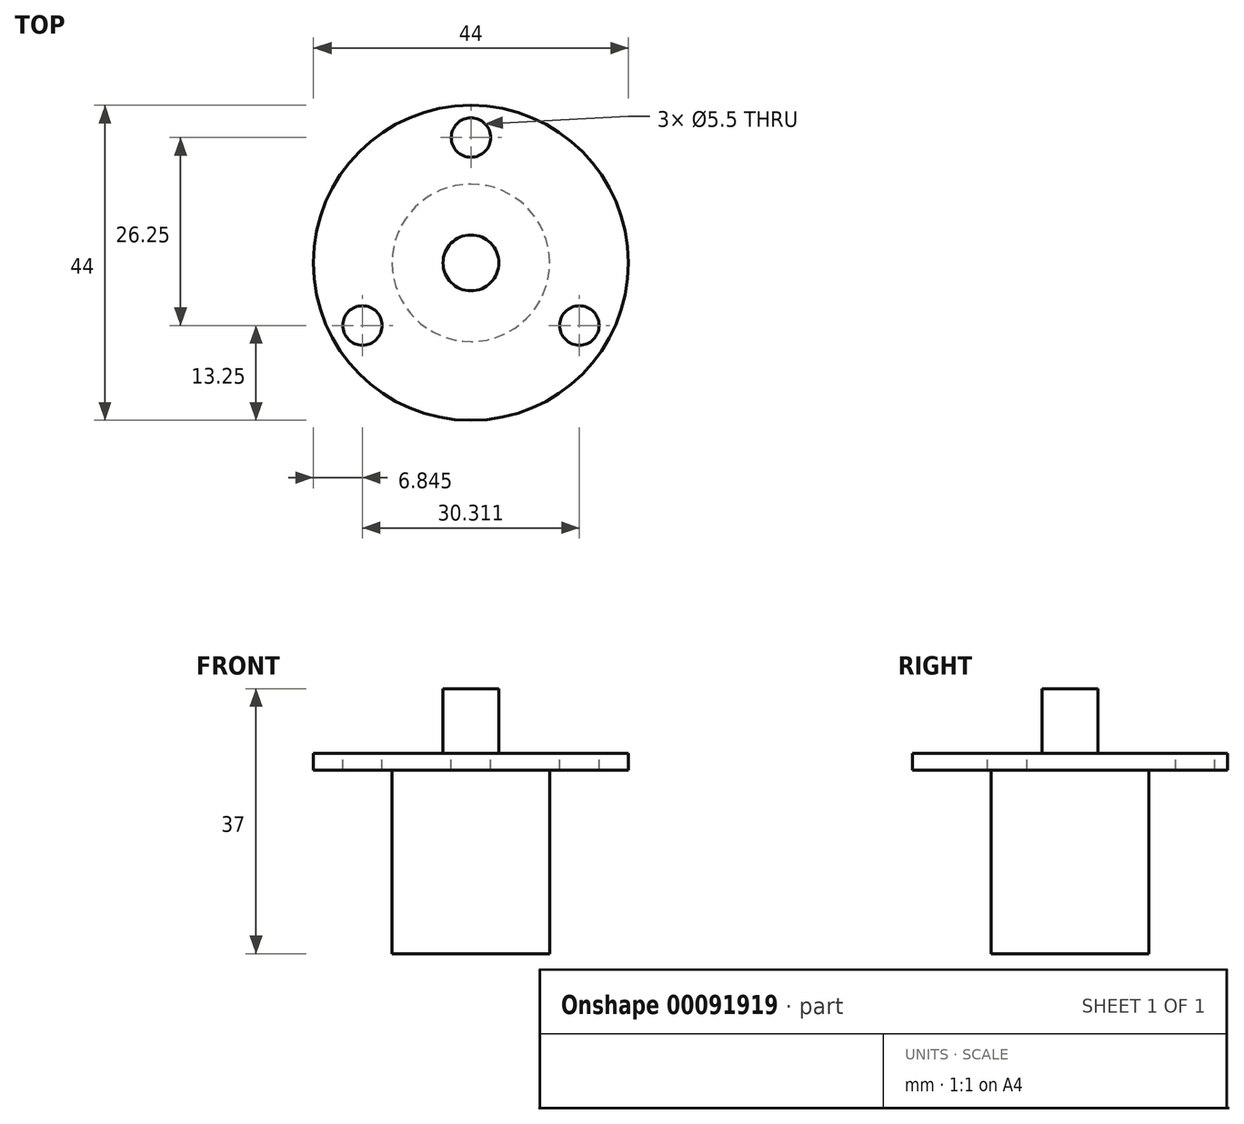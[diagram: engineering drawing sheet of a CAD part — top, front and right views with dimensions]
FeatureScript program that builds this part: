
annotation { "Feature Type Name" : "Feature", "Feature Type Description" : "" }
export const myFeature = defineFeature(function(context is Context, id is Id, definition is map)
    precondition{}
    {
        {
            var Q0;
            Q0=qCreatedBy(makeId("Top.planeOp"),FACE);
            var sketch = newSketch(context, id + "F0", { "sketchPlane" : qUnion([Q0])});
            skCircle(sketch, "E0", {"center": v(0, 0) * mm, "radius": 11 * mm});
            skSolve(sketch);
        }
        {
            var Q0;
            Q0 = qSketchRegion(id + "F0", true);
            extrude(context, id + "F1", {"entities" : qUnion([Q0]), "oppositeDirection" : true, "depth" : 28 * mm});
        }
        {
            var Q0;
            Q0=qCreatedBy(makeId("Top.planeOp"),FACE);
            var sketch = newSketch(context, id + "F2", { "sketchPlane" : qUnion([Q0])});
            skCircle(sketch, "E1", {"center": v(0, 0) * mm, "radius": 22 * mm});
            skSolve(sketch);
        }
        {
            var Q0;
            Q0 = qSketchRegion(id + "F2", true);
            extrude(context, id + "F3", {"entities" : qUnion([Q0]), "operationType" : NewBodyOperationType.ADD, "oppositeDirection" : true, "depth" : 2.4 * mm});
        }
        {
            var Q0;
            Q0=makeQuery(id+"F3.boolean.opBoolean","MERGE",FACE,{"derivedFrom":[makeQuery(id+"F1.opExtrude","CAP_FACE",FACE,{"disambiguationData":[OSD([sQuery(id+"F0.wireOp",EDGE,"E0")])],"isStart":true}),makeQuery(id+"F3.opExtrude","CAP_FACE",FACE,{"disambiguationData":[OSD([sQuery(id+"F2.wireOp",EDGE,"E1")])],"isStart":true})]});
            var sketch = newSketch(context, id + "F4", { "sketchPlane" : qUnion([Q0])});
            skCircle(sketch, "E2", {"center": v(0, 17.5) * mm, "radius": 2.75 * mm});
            skCircle(sketch, "E3", {"center": v(0, 0) * mm, "radius": 17.5 * mm, "construction": true});
            skCircle(sketch, "E4.1.0", {"center": v(-15.16, -8.75) * mm, "radius": 2.75 * mm});
            skCircle(sketch, "E4.2.0", {"center": v(15.16, -8.75) * mm, "radius": 2.75 * mm});
            skSolve(sketch);
        }
        {
            var Q0;
            Q0 = qSketchRegion(id + "F4", true);
            extrude(context, id + "F5", {"entities" : qUnion([Q0]), "operationType" : NewBodyOperationType.REMOVE, "endBound" : BoundingType.THROUGH_ALL, "oppositeDirection" : true, "depth" : 25 * mm});
        }
        {
            var Q0;
            Q0=makeQuery(id+"F3.boolean.opBoolean","MERGE",FACE,{"derivedFrom":[makeQuery(id+"F1.opExtrude","CAP_FACE",FACE,{"disambiguationData":[OSD([sQuery(id+"F0.wireOp",EDGE,"E0")])],"isStart":true}),makeQuery(id+"F3.opExtrude","CAP_FACE",FACE,{"disambiguationData":[OSD([sQuery(id+"F2.wireOp",EDGE,"E1")])],"isStart":true})]});
            var sketch = newSketch(context, id + "F6", { "sketchPlane" : qUnion([Q0])});
            skCircle(sketch, "E5", {"center": v(0, 0) * mm, "radius": 3.9 * mm});
            skSolve(sketch);
        }
        {
            var Q0;
            Q0 = qSketchRegion(id + "F6", true);
            extrude(context, id + "F7", {"entities" : qUnion([Q0]), "operationType" : NewBodyOperationType.ADD, "depth" : 9 * mm});
        }
    });
